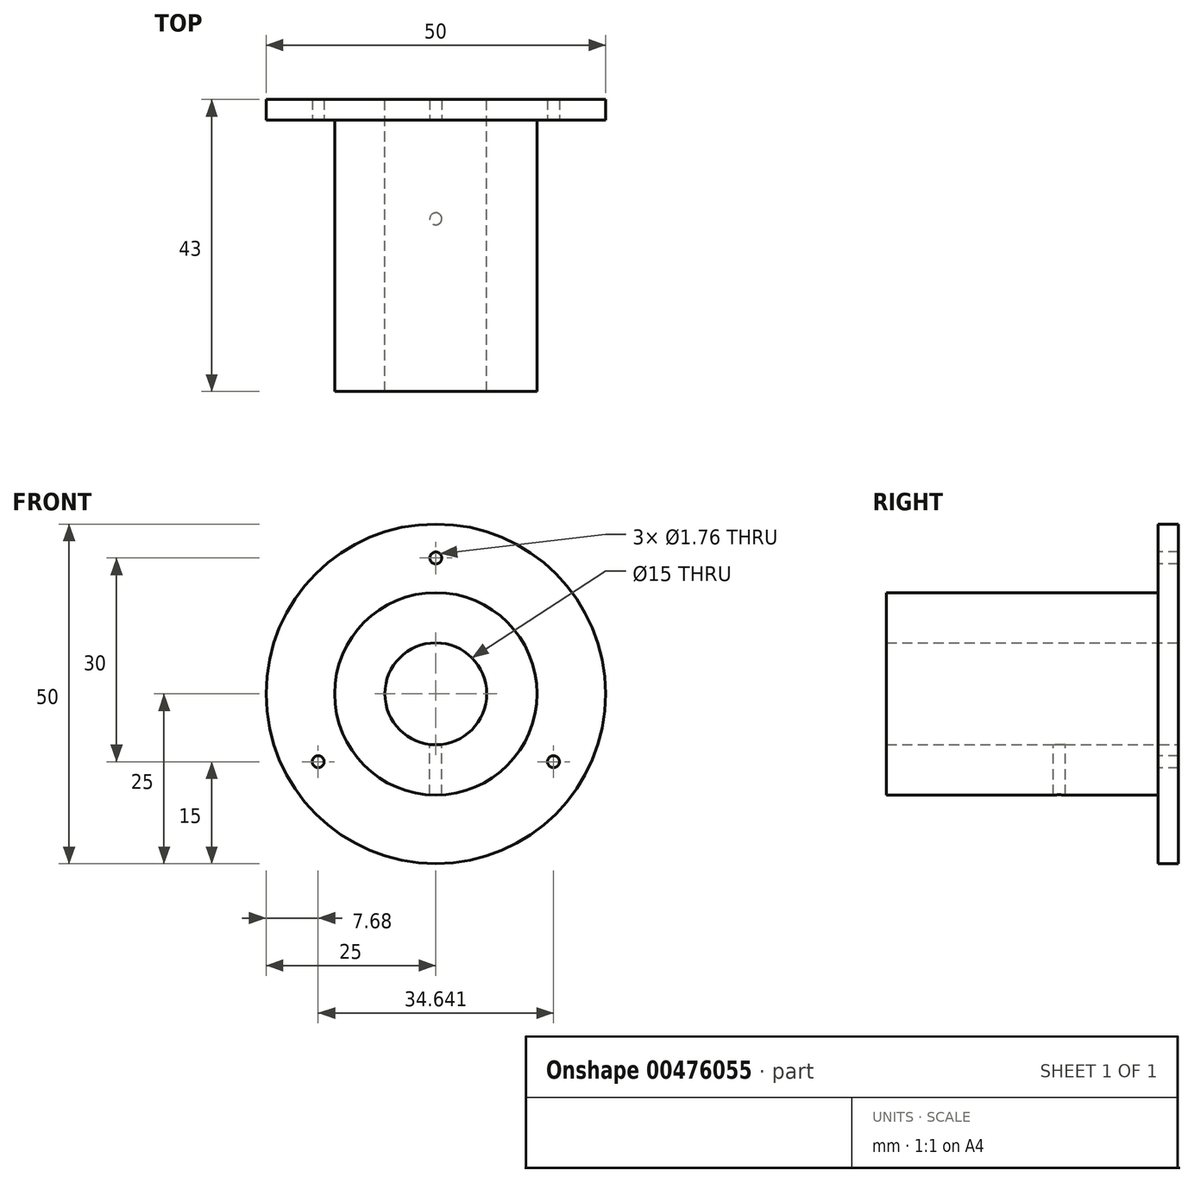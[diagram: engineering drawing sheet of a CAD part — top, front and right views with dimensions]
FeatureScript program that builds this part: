
annotation { "Feature Type Name" : "Feature", "Feature Type Description" : "" }
export const myFeature = defineFeature(function(context is Context, id is Id, definition is map)
    precondition{}
    {
        {
            var Q0;
            Q0=qCreatedBy(makeId("Front.planeOp"),FACE);
            var sketch = newSketch(context, id + "F0", { "sketchPlane" : qUnion([Q0])});
            skCircle(sketch, "E0", {"center": v(0, 0) * mm, "radius": 14.9 * mm});
            skCircle(sketch, "E1", {"center": v(0, 0) * mm, "radius": 7.5 * mm});
            skCircle(sketch, "E2", {"center": v(0, 0) * mm, "radius": 25 * mm});
            skCircle(sketch, "E3", {"center": v(0, 20) * mm, "radius": 0.88 * mm});
            skCircle(sketch, "E4.1.0", {"center": v(-17.32, -10) * mm, "radius": 0.88 * mm});
            skCircle(sketch, "E4.2.0", {"center": v(17.32, -10) * mm, "radius": 0.88 * mm});
            skSolve(sketch);
        }
        {
            var Q0;
            Q0=makeQuery(id+"F0.imprint","IMPRINT",FACE,{"disambiguationData":[TD([[makeQuery(id+"F0.imprint","IMPRINT",EDGE,{"derivedFrom":sQuery(id+"F0.wireOp",EDGE,"E0")}),1.0]])]});
            extrude(context, id + "F1", {"entities" : qUnion([Q0]), "depth" : 40 * mm});
        }
        {
            var Q0;
            Q0=makeQuery(id+"F0.imprint","IMPRINT",FACE,{"disambiguationData":[TD([[makeQuery(id+"F0.imprint","IMPRINT",EDGE,{"derivedFrom":sQuery(id+"F0.wireOp",EDGE,"E0")}),-1.0]])]});
            var Q1;
            Q1=makeQuery(id+"F0.imprint","IMPRINT",FACE,{"disambiguationData":[TD([[makeQuery(id+"F0.imprint","IMPRINT",EDGE,{"derivedFrom":sQuery(id+"F0.wireOp",EDGE,"E0")}),1.0]])]});
            extrude(context, id + "F2", {"entities" : qUnion([Q0, Q1]), "operationType" : NewBodyOperationType.ADD, "oppositeDirection" : true, "depth" : 3 * mm});
        }
        {
            var Q0;
            Q0=qCreatedBy(makeId("Top.planeOp"),FACE);
            var sketch = newSketch(context, id + "F3", { "sketchPlane" : qUnion([Q0])});
            skCircle(sketch, "E5", {"center": v(0, -14.56) * mm, "radius": 0.88 * mm});
            skSolve(sketch);
        }
        {
            var Q0;
            Q0 = qSketchRegion(id + "F3", true);
            extrude(context, id + "F4", {"entities" : qUnion([Q0]), "operationType" : NewBodyOperationType.REMOVE, "oppositeDirection" : true, "depth" : 25 * mm});
        }
    });
